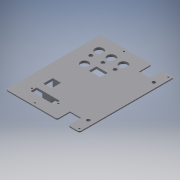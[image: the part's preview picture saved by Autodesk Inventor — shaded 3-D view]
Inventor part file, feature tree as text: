
AUTODESK INVENTOR PART (.ipt)
format: ipt  version: 2016 (Build 200138000, 138)  size: 335,360 bytes
history: native  units: in
note: dims shown in document units (in); Inventor stores cm internally (conversion verified against a paired STEP export)
features: extrude x7, sketch x7, fillet x1, projected_geometry x1
ambient origin geometry x8: Origin, YZ Plane, XZ Plane, XY Plane, X Axis, Y Axis, Z Axis, Center Point
bodies: Solid1 (feature_tree)
feature tree (16):
  extrude  "Extrusion1"  Depth=0.6299in
  extrude  "Extrusion2"  Depth=6.5354in
  extrude  "Extrusion8"  Depth=1.063in
  fillet  "Fillet1"  Radius=0.0394in
  extrude  "Extrusion9"  Depth=0.0394in
  extrude  "Extrusion10"  Depth=0.0394in
  extrude  "Extrusion12"  Depth=0.1181in
  extrude  "Extrusion13"  Depth=0.1181in
  sketch  "Sketch1"  dims[d0=0.9449in d1=0.6299in]
  sketch  "Sketch2"  dims[d2=3.4612in d3=6.5354in]
  sketch  "Sketch9"  dims[d4=0.1181in d5=1.063in d6=0.0394in]
  sketch  "Sketch10"  dims[d8=0.0394in d9=0.0394in]
  sketch  "Sketch11"  dims[d10=0.0394in d11=0.0394in]
  sketch  "Sketch15"  dims[d12=0.0787in d13=0.0in d14=0.1181in]
  sketch  "Sketch16"  dims[d15=0.1181in d16=0.1181in d17=0.2756in d18=0.1181in d19=0.1181in d20=0.0787in d21=0.0in d62=0.1181in d63=0.2362in d64=0.1181in d69=0.7874in d70=0.6693in d71=0.5709in d85=0.5906in d97=0.4331in d98=1.6339in d99=0.2953in d100=0.1181in d101=0.1181in d102=0.1181in d103=0.1181in d104=0.5906in d105=0.0in d106=1.0177in d108=0.0in d111=0.1181in d112=0.0787in d113=0.0787in d114=0.0787in d115=0.6693in d116=0.0in d117=0.0787in d118=0.0787in d120=0.0315in d121=0.0472in d122=0.315in d123=0.0in d130=0.2008in d131=4.3307in d132=1.1811in d133=0.0787in d134=0.0in d143=0.1927in d146=0.06in d151=0.1181in d152=0.1181in d153=0.3346in d154=0.3346in d155=0.0787in d156=0.0in d157=1.9685in d158=0.5906in d159=0.5906in d160=0.5906in d161=0.8583in d162=0.8583in d163=0.5906in d164=0.5906in d165=0.5906in d166=1.9685in d167=1.9685in d168=0.5906in d169=0.2559in d171=0.7874in d172=0.5315in d173=0.5512in d174=0.5906in d175=0.9055in d177=0.3346in]
  projected_geometry  "Projected Loop1"
